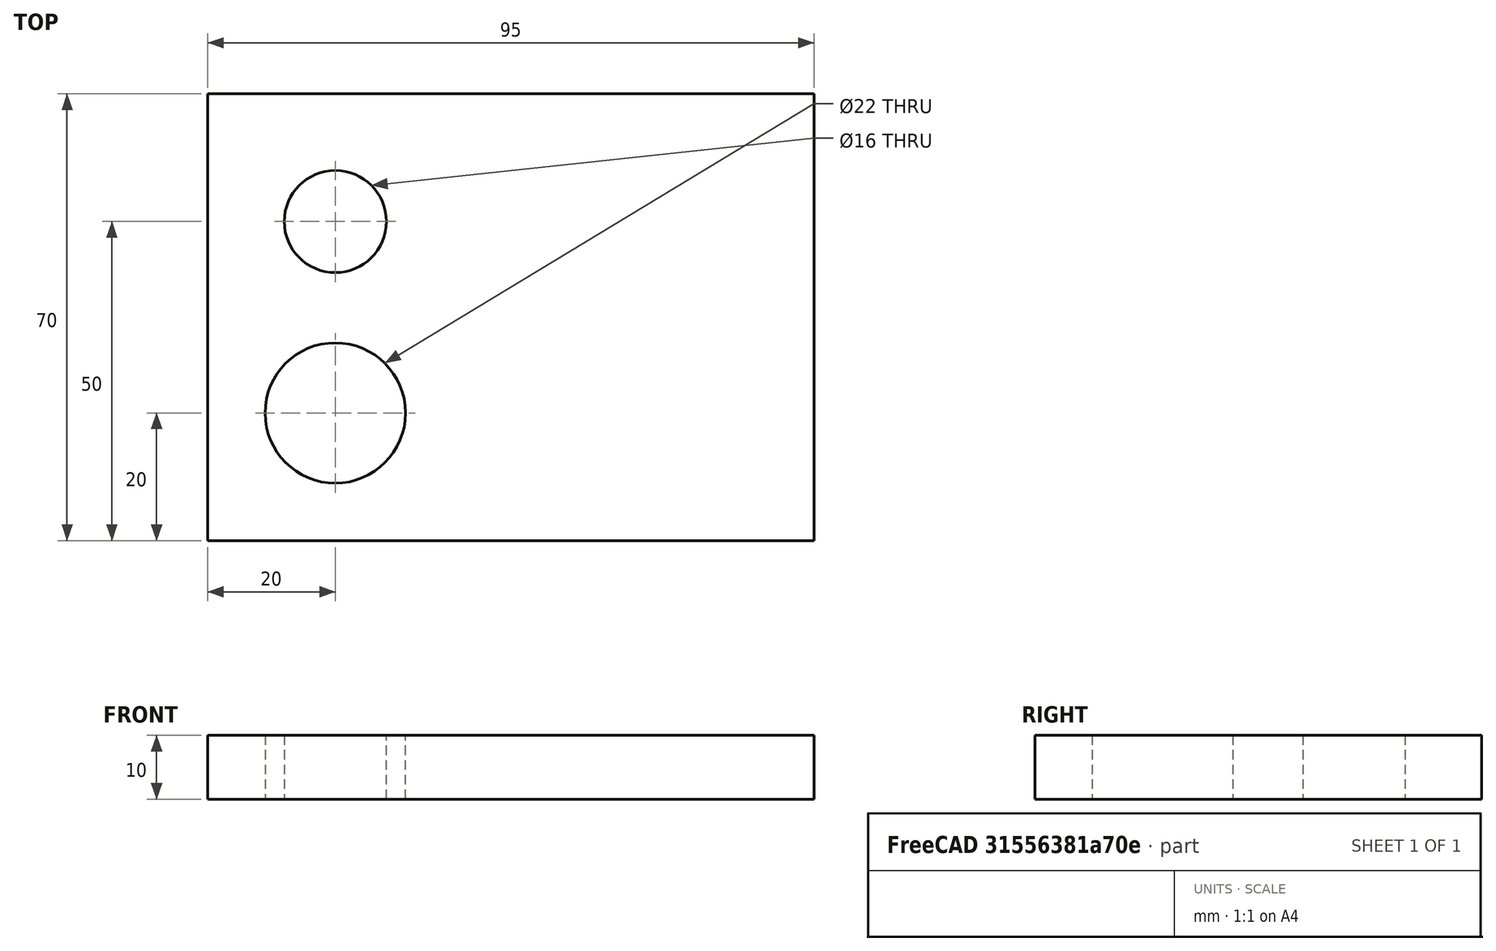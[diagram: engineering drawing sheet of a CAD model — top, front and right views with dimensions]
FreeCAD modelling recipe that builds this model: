
FCSTD DOCUMENT  (FreeCAD 0.19R24276 (Git))
Label: BLDC_holder_part1
License: All rights reserved
LicenseURL: http://en.wikipedia.org/wiki/All_rights_reserved
objects: Sketcher::SketchObject×1, PartDesign::Pad×1, PartDesign::Body×1
note: 4 computed .brp shape members not serialized (recipe doc carries the construction recipe); baked Part::Feature solids carry a one-line shape summary decoded from their .brp

FEATURE [Sketcher::SketchObject] Sketch
  FullyConstrained = true
  MapMode = 5
  Support = -> [XY_Plane]
  sketch-geometry (6):
    g0: Circle CenterX=0 CenterY=0 CenterZ=0 NormalX=0 NormalY=0 NormalZ=1 AngleXU=0 Radius=8
    g1: Circle CenterX=0 CenterY=-30 CenterZ=0 NormalX=0 NormalY=0 NormalZ=1 AngleXU=0 Radius=11
    g2: LineSegment StartX=-20 StartY=20 StartZ=0 EndX=75 EndY=20 EndZ=0
    g3: LineSegment StartX=75 StartY=20 StartZ=0 EndX=75 EndY=-50 EndZ=0
    g4: LineSegment StartX=75 StartY=-50 StartZ=0 EndX=-20 EndY=-50 EndZ=0
    g5: LineSegment StartX=-20 StartY=-50 StartZ=0 EndX=-20 EndY=20 EndZ=0
  constraints (17):
    c: Coincident(g0,g-1)
    c: Diameter(g0) = 16
    c: PointOnObject(g1,g-2)
    c: Diameter(g1) = 22
    c: DistanceY(g1,g0) = 30
    c: Coincident(g2,g3)
    c: Coincident(g3,g4)
    c: Coincident(g4,g5)
    c: Coincident(g5,g2)
    c: Horizontal(g2)
    c: Horizontal(g4)
    c: Vertical(g3)
    c: Vertical(g5)
    c: DistanceX(g0,g2) = 75
    c: DistanceY(g0,g2) = 20
    c: DistanceY(g4,g1) = 20
    c: DistanceX(g2,g0) = 20
FEATURE [PartDesign::Pad] Pad
  Direction = (1,1,1)
  Length = 10
  Length2 = 100
  Profile = -> Sketch
  Type = 0
FEATURE [PartDesign::Body] Body
  Group = -> [Sketch,Pad]
  Origin = -> Origin
  Tip = -> Pad
